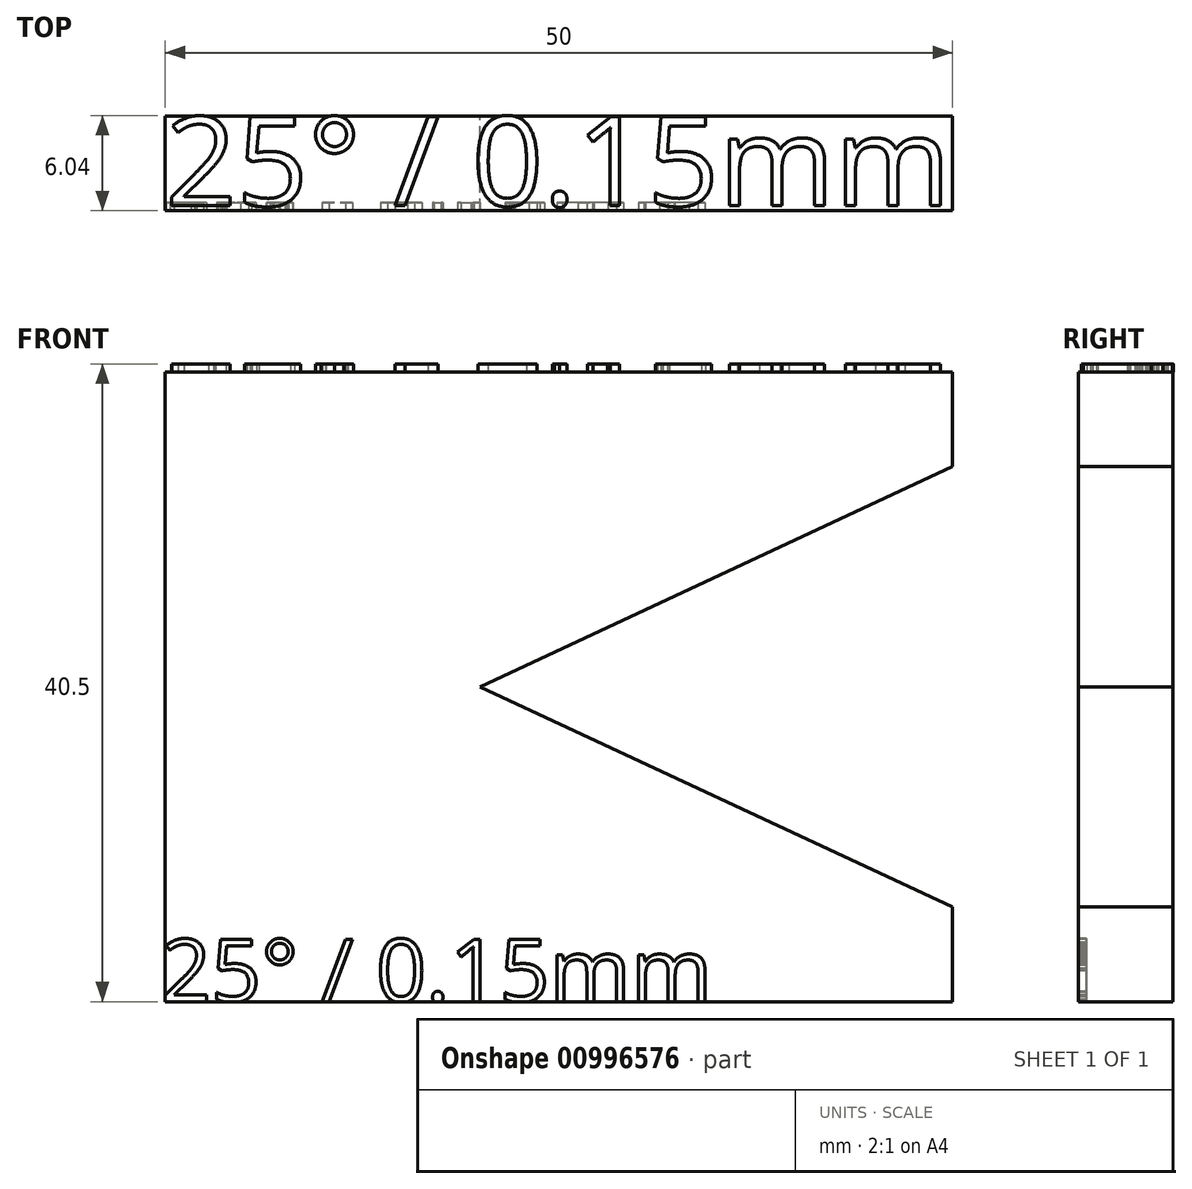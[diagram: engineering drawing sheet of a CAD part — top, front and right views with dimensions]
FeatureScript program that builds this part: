
annotation { "Feature Type Name" : "Feature", "Feature Type Description" : "" }
export const myFeature = defineFeature(function(context is Context, id is Id, definition is map)
    precondition{}
    {
        {
            var Q0;
            Q0=qCreatedBy(makeId("Front.planeOp"),FACE);
            var sketch = newSketch(context, id + "F0", { "sketchPlane" : qUnion([Q0])});
            skLineSegment(sketch, "E0", {"start": v(0, 39.45) * mm, "end": v(0, -35.1) * mm, "construction": true});
            skLineSegment(sketch, "E1", {"start": v(-35.77, 0) * mm, "end": v(35.97, 0) * mm, "construction": true});
            skLineSegment(sketch, "E2", {"start": v(-20, 20) * mm, "end": v(-20, -20) * mm});
            skLineSegment(sketch, "E3", {"start": v(-20, -20) * mm, "end": v(30, -20) * mm});
            skLineSegment(sketch, "E4", {"start": v(0, 0) * mm, "end": v(30, -13.99) * mm});
            skLineSegment(sketch, "E5", {"start": v(30, -13.99) * mm, "end": v(30, -20) * mm});
            skLineSegment(sketch, "E6.MirrorCS", {"start": v(0, 0) * mm, "end": v(30, 13.99) * mm});
            skLineSegment(sketch, "E7.MirrorCS", {"start": v(30, 13.99) * mm, "end": v(30, 20) * mm});
            skLineSegment(sketch, "E8.MirrorCS", {"start": v(-20, 20) * mm, "end": v(30, 20) * mm});
            skSolve(sketch);
        }
        {
            var Q0;
            Q0=makeQuery(id+"F0.imprint","IMPRINT",FACE,{"disambiguationData":[TD([[makeQuery(id+"F0.imprint","IMPRINT",EDGE,{"derivedFrom":sQuery(id+"F0.wireOp",EDGE,"E2")}),1.0]])]});
            extrude(context, id + "F1", {"entities" : qUnion([Q0]), "depth" : 6 * mm, "offsetDistance" : 25 * mm});
        }
        {
            var Q0;
            Q0=makeQuery(id+"F1.opExtrude","SWEPT_FACE",FACE,{"disambiguationData":[OSD([sQuery(id+"F0.wireOp",EDGE,"E8.MirrorCS")])]});
            var sketch = newSketch(context, id + "F2", { "sketchPlane" : qUnion([Q0])});
            skText(sketch, "E9", { "text": "25° / 0.15mm", "fontName": "OpenSans-Regular.ttf"});
            const initialGuessF2  = {"E9": [-0.02, -0.0057, 1, 0, 0.0057]};
            skSetInitialGuess(sketch, initialGuessF2);
            skSolve(sketch);
        }
        {
            var Q0;
            Q0=qSketchRegion(id+"F2",true);
            extrude(context, id + "F3", {"entities" : qUnion([Q0]), "operationType" : NewBodyOperationType.ADD, "depth" : 0.5 * mm, "offsetDistance" : 25 * mm});
        }
        {
            var Q0;
            Q0=makeQuery(id+"F1.opExtrude","SWEPT_FACE",FACE,{"disambiguationData":[OSD([sQuery(id+"F0.wireOp",EDGE,"E2")])]});
            var sketch = newSketch(context, id + "F4", { "sketchPlane" : qUnion([Q0])});
            skText(sketch, "E10", { "text": "25° / 0.15mm", "fontName": "OpenSans-Regular.ttf"});
            const initialGuessF4  = {"E10": [0, -0.024, 1, 0, 0.004]};
            skSetInitialGuess(sketch, initialGuessF4);
            skSolve(sketch);
        }
        {
            var Q0;
            Q0=qSketchRegion(id+"F4",true);
            extrude(context, id + "F5", {"entities" : qUnion([Q0]), "oppositeDirection" : true, "depth" : 0.5 * mm, "offsetDistance" : 25 * mm});
        }
        {
            var Q0;
            Q0=makeQuery(id+"F5.opExtrude","SWEPT_BODY",BODY,{"disambiguationData":[OSD([sQuery(id+"F4.wireOp",EDGE,"E10.sketch_text.stroke-0"),sQuery(id+"F4.wireOp",EDGE,"E10.sketch_text.stroke-1"),sQuery(id+"F4.wireOp",EDGE,"E10.sketch_text.stroke-2"),sQuery(id+"F4.wireOp",EDGE,"E10.sketch_text.stroke-3"),sQuery(id+"F4.wireOp",EDGE,"E10.sketch_text.stroke-4"),sQuery(id+"F4.wireOp",EDGE,"E10.sketch_text.stroke-5"),sQuery(id+"F4.wireOp",EDGE,"E10.sketch_text.stroke-6"),sQuery(id+"F4.wireOp",EDGE,"E10.sketch_text.stroke-7"),sQuery(id+"F4.wireOp",EDGE,"E10.sketch_text.stroke-8"),sQuery(id+"F4.wireOp",EDGE,"E10.sketch_text.stroke-9"),sQuery(id+"F4.wireOp",EDGE,"E10.sketch_text.stroke-10"),sQuery(id+"F4.wireOp",EDGE,"E10.sketch_text.stroke-11"),sQuery(id+"F4.wireOp",EDGE,"E10.sketch_text.stroke-12"),sQuery(id+"F4.wireOp",EDGE,"E10.sketch_text.stroke-13"),sQuery(id+"F4.wireOp",EDGE,"E10.sketch_text.stroke-14"),sQuery(id+"F4.wireOp",EDGE,"E10.sketch_text.stroke-15"),sQuery(id+"F4.wireOp",EDGE,"E10.sketch_text.stroke-16"),sQuery(id+"F4.wireOp",EDGE,"E10.sketch_text.stroke-17"),sQuery(id+"F4.wireOp",EDGE,"E10.sketch_text.stroke-18"),sQuery(id+"F4.wireOp",EDGE,"E10.sketch_text.stroke-19")])]});
            var Q1;
            Q1=makeQuery(id+"F5.opExtrude","SWEPT_BODY",BODY,{"disambiguationData":[OSD([sQuery(id+"F4.wireOp",EDGE,"E10.sketch_text.stroke-20"),sQuery(id+"F4.wireOp",EDGE,"E10.sketch_text.stroke-21"),sQuery(id+"F4.wireOp",EDGE,"E10.sketch_text.stroke-22"),sQuery(id+"F4.wireOp",EDGE,"E10.sketch_text.stroke-23"),sQuery(id+"F4.wireOp",EDGE,"E10.sketch_text.stroke-24"),sQuery(id+"F4.wireOp",EDGE,"E10.sketch_text.stroke-25"),sQuery(id+"F4.wireOp",EDGE,"E10.sketch_text.stroke-26"),sQuery(id+"F4.wireOp",EDGE,"E10.sketch_text.stroke-27"),sQuery(id+"F4.wireOp",EDGE,"E10.sketch_text.stroke-28"),sQuery(id+"F4.wireOp",EDGE,"E10.sketch_text.stroke-29"),sQuery(id+"F4.wireOp",EDGE,"E10.sketch_text.stroke-30"),sQuery(id+"F4.wireOp",EDGE,"E10.sketch_text.stroke-31"),sQuery(id+"F4.wireOp",EDGE,"E10.sketch_text.stroke-32"),sQuery(id+"F4.wireOp",EDGE,"E10.sketch_text.stroke-33"),sQuery(id+"F4.wireOp",EDGE,"E10.sketch_text.stroke-34"),sQuery(id+"F4.wireOp",EDGE,"E10.sketch_text.stroke-35"),sQuery(id+"F4.wireOp",EDGE,"E10.sketch_text.stroke-36"),sQuery(id+"F4.wireOp",EDGE,"E10.sketch_text.stroke-37"),sQuery(id+"F4.wireOp",EDGE,"E10.sketch_text.stroke-38")])]});
            var Q2;
            Q2=makeQuery(id+"F5.opExtrude","SWEPT_BODY",BODY,{"disambiguationData":[OSD([sQuery(id+"F4.wireOp",EDGE,"E10.sketch_text.stroke-39"),sQuery(id+"F4.wireOp",EDGE,"E10.sketch_text.stroke-40"),sQuery(id+"F4.wireOp",EDGE,"E10.sketch_text.stroke-41"),sQuery(id+"F4.wireOp",EDGE,"E10.sketch_text.stroke-42"),sQuery(id+"F4.wireOp",EDGE,"E10.sketch_text.stroke-43"),sQuery(id+"F4.wireOp",EDGE,"E10.sketch_text.stroke-44"),sQuery(id+"F4.wireOp",EDGE,"E10.sketch_text.stroke-45"),sQuery(id+"F4.wireOp",EDGE,"E10.sketch_text.stroke-46"),sQuery(id+"F4.wireOp",EDGE,"E10.sketch_text.stroke-47"),sQuery(id+"F4.wireOp",EDGE,"E10.sketch_text.stroke-48"),sQuery(id+"F4.wireOp",EDGE,"E10.sketch_text.stroke-49"),sQuery(id+"F4.wireOp",EDGE,"E10.sketch_text.stroke-50"),sQuery(id+"F4.wireOp",EDGE,"E10.sketch_text.stroke-51"),sQuery(id+"F4.wireOp",EDGE,"E10.sketch_text.stroke-52"),sQuery(id+"F4.wireOp",EDGE,"E10.sketch_text.stroke-53"),sQuery(id+"F4.wireOp",EDGE,"E10.sketch_text.stroke-54"),sQuery(id+"F4.wireOp",EDGE,"E10.sketch_text.stroke-55")])]});
            var Q3;
            Q3=makeQuery(id+"F5.opExtrude","SWEPT_BODY",BODY,{"disambiguationData":[OSD([sQuery(id+"F4.wireOp",EDGE,"E10.sketch_text.stroke-56"),sQuery(id+"F4.wireOp",EDGE,"E10.sketch_text.stroke-57"),sQuery(id+"F4.wireOp",EDGE,"E10.sketch_text.stroke-58"),sQuery(id+"F4.wireOp",EDGE,"E10.sketch_text.stroke-59")])]});
            var Q4;
            Q4=makeQuery(id+"F5.opExtrude","SWEPT_BODY",BODY,{"disambiguationData":[OSD([sQuery(id+"F4.wireOp",EDGE,"E10.sketch_text.stroke-60"),sQuery(id+"F4.wireOp",EDGE,"E10.sketch_text.stroke-61"),sQuery(id+"F4.wireOp",EDGE,"E10.sketch_text.stroke-62"),sQuery(id+"F4.wireOp",EDGE,"E10.sketch_text.stroke-63"),sQuery(id+"F4.wireOp",EDGE,"E10.sketch_text.stroke-64"),sQuery(id+"F4.wireOp",EDGE,"E10.sketch_text.stroke-65"),sQuery(id+"F4.wireOp",EDGE,"E10.sketch_text.stroke-66"),sQuery(id+"F4.wireOp",EDGE,"E10.sketch_text.stroke-67"),sQuery(id+"F4.wireOp",EDGE,"E10.sketch_text.stroke-68"),sQuery(id+"F4.wireOp",EDGE,"E10.sketch_text.stroke-69"),sQuery(id+"F4.wireOp",EDGE,"E10.sketch_text.stroke-70"),sQuery(id+"F4.wireOp",EDGE,"E10.sketch_text.stroke-71"),sQuery(id+"F4.wireOp",EDGE,"E10.sketch_text.stroke-72"),sQuery(id+"F4.wireOp",EDGE,"E10.sketch_text.stroke-73"),sQuery(id+"F4.wireOp",EDGE,"E10.sketch_text.stroke-74"),sQuery(id+"F4.wireOp",EDGE,"E10.sketch_text.stroke-75")])]});
            var Q5;
            Q5=makeQuery(id+"F5.opExtrude","SWEPT_BODY",BODY,{"disambiguationData":[OSD([sQuery(id+"F4.wireOp",EDGE,"E10.sketch_text.stroke-76"),sQuery(id+"F4.wireOp",EDGE,"E10.sketch_text.stroke-77"),sQuery(id+"F4.wireOp",EDGE,"E10.sketch_text.stroke-78"),sQuery(id+"F4.wireOp",EDGE,"E10.sketch_text.stroke-79"),sQuery(id+"F4.wireOp",EDGE,"E10.sketch_text.stroke-80"),sQuery(id+"F4.wireOp",EDGE,"E10.sketch_text.stroke-81"),sQuery(id+"F4.wireOp",EDGE,"E10.sketch_text.stroke-82"),sQuery(id+"F4.wireOp",EDGE,"E10.sketch_text.stroke-83")])]});
            var Q6;
            Q6=makeQuery(id+"F5.opExtrude","SWEPT_BODY",BODY,{"disambiguationData":[OSD([sQuery(id+"F4.wireOp",EDGE,"E10.sketch_text.stroke-84"),sQuery(id+"F4.wireOp",EDGE,"E10.sketch_text.stroke-85"),sQuery(id+"F4.wireOp",EDGE,"E10.sketch_text.stroke-86"),sQuery(id+"F4.wireOp",EDGE,"E10.sketch_text.stroke-87"),sQuery(id+"F4.wireOp",EDGE,"E10.sketch_text.stroke-88"),sQuery(id+"F4.wireOp",EDGE,"E10.sketch_text.stroke-89"),sQuery(id+"F4.wireOp",EDGE,"E10.sketch_text.stroke-90"),sQuery(id+"F4.wireOp",EDGE,"E10.sketch_text.stroke-91"),sQuery(id+"F4.wireOp",EDGE,"E10.sketch_text.stroke-92")])]});
            var Q7;
            Q7=makeQuery(id+"F5.opExtrude","SWEPT_BODY",BODY,{"disambiguationData":[OSD([sQuery(id+"F4.wireOp",EDGE,"E10.sketch_text.stroke-93"),sQuery(id+"F4.wireOp",EDGE,"E10.sketch_text.stroke-94"),sQuery(id+"F4.wireOp",EDGE,"E10.sketch_text.stroke-95"),sQuery(id+"F4.wireOp",EDGE,"E10.sketch_text.stroke-96"),sQuery(id+"F4.wireOp",EDGE,"E10.sketch_text.stroke-97"),sQuery(id+"F4.wireOp",EDGE,"E10.sketch_text.stroke-98"),sQuery(id+"F4.wireOp",EDGE,"E10.sketch_text.stroke-99"),sQuery(id+"F4.wireOp",EDGE,"E10.sketch_text.stroke-100"),sQuery(id+"F4.wireOp",EDGE,"E10.sketch_text.stroke-101"),sQuery(id+"F4.wireOp",EDGE,"E10.sketch_text.stroke-102"),sQuery(id+"F4.wireOp",EDGE,"E10.sketch_text.stroke-103"),sQuery(id+"F4.wireOp",EDGE,"E10.sketch_text.stroke-104"),sQuery(id+"F4.wireOp",EDGE,"E10.sketch_text.stroke-105"),sQuery(id+"F4.wireOp",EDGE,"E10.sketch_text.stroke-106"),sQuery(id+"F4.wireOp",EDGE,"E10.sketch_text.stroke-107"),sQuery(id+"F4.wireOp",EDGE,"E10.sketch_text.stroke-108"),sQuery(id+"F4.wireOp",EDGE,"E10.sketch_text.stroke-109"),sQuery(id+"F4.wireOp",EDGE,"E10.sketch_text.stroke-110"),sQuery(id+"F4.wireOp",EDGE,"E10.sketch_text.stroke-111"),sQuery(id+"F4.wireOp",EDGE,"E10.sketch_text.stroke-112"),sQuery(id+"F4.wireOp",EDGE,"E10.sketch_text.stroke-113"),sQuery(id+"F4.wireOp",EDGE,"E10.sketch_text.stroke-114"),sQuery(id+"F4.wireOp",EDGE,"E10.sketch_text.stroke-115"),sQuery(id+"F4.wireOp",EDGE,"E10.sketch_text.stroke-116"),sQuery(id+"F4.wireOp",EDGE,"E10.sketch_text.stroke-117"),sQuery(id+"F4.wireOp",EDGE,"E10.sketch_text.stroke-118"),sQuery(id+"F4.wireOp",EDGE,"E10.sketch_text.stroke-119"),sQuery(id+"F4.wireOp",EDGE,"E10.sketch_text.stroke-120")])]});
            var Q8;
            Q8=makeQuery(id+"F5.opExtrude","SWEPT_BODY",BODY,{"disambiguationData":[OSD([sQuery(id+"F4.wireOp",EDGE,"E10.sketch_text.stroke-121"),sQuery(id+"F4.wireOp",EDGE,"E10.sketch_text.stroke-122"),sQuery(id+"F4.wireOp",EDGE,"E10.sketch_text.stroke-123"),sQuery(id+"F4.wireOp",EDGE,"E10.sketch_text.stroke-124"),sQuery(id+"F4.wireOp",EDGE,"E10.sketch_text.stroke-125"),sQuery(id+"F4.wireOp",EDGE,"E10.sketch_text.stroke-126"),sQuery(id+"F4.wireOp",EDGE,"E10.sketch_text.stroke-127"),sQuery(id+"F4.wireOp",EDGE,"E10.sketch_text.stroke-128"),sQuery(id+"F4.wireOp",EDGE,"E10.sketch_text.stroke-129"),sQuery(id+"F4.wireOp",EDGE,"E10.sketch_text.stroke-130"),sQuery(id+"F4.wireOp",EDGE,"E10.sketch_text.stroke-131"),sQuery(id+"F4.wireOp",EDGE,"E10.sketch_text.stroke-132"),sQuery(id+"F4.wireOp",EDGE,"E10.sketch_text.stroke-133"),sQuery(id+"F4.wireOp",EDGE,"E10.sketch_text.stroke-134"),sQuery(id+"F4.wireOp",EDGE,"E10.sketch_text.stroke-135"),sQuery(id+"F4.wireOp",EDGE,"E10.sketch_text.stroke-136"),sQuery(id+"F4.wireOp",EDGE,"E10.sketch_text.stroke-137"),sQuery(id+"F4.wireOp",EDGE,"E10.sketch_text.stroke-138"),sQuery(id+"F4.wireOp",EDGE,"E10.sketch_text.stroke-139"),sQuery(id+"F4.wireOp",EDGE,"E10.sketch_text.stroke-140"),sQuery(id+"F4.wireOp",EDGE,"E10.sketch_text.stroke-141"),sQuery(id+"F4.wireOp",EDGE,"E10.sketch_text.stroke-142"),sQuery(id+"F4.wireOp",EDGE,"E10.sketch_text.stroke-143"),sQuery(id+"F4.wireOp",EDGE,"E10.sketch_text.stroke-144"),sQuery(id+"F4.wireOp",EDGE,"E10.sketch_text.stroke-145"),sQuery(id+"F4.wireOp",EDGE,"E10.sketch_text.stroke-146"),sQuery(id+"F4.wireOp",EDGE,"E10.sketch_text.stroke-147"),sQuery(id+"F4.wireOp",EDGE,"E10.sketch_text.stroke-148")])]});
            var Q9;
            Q9=makeQuery(id+"F5.opExtrude","SWEPT_BODY",BODY,{"disambiguationData":[OSD([sQuery(id+"F4.wireOp",EDGE,"E10.sketch_text.stroke-140"),sQuery(id+"F4.wireOp",EDGE,"E10.sketch_text.stroke-141"),sQuery(id+"F4.wireOp",EDGE,"E10.sketch_text.stroke-142"),sQuery(id+"F4.wireOp",EDGE,"E10.sketch_text.stroke-143"),sQuery(id+"F4.wireOp",EDGE,"E10.sketch_text.stroke-144"),sQuery(id+"F4.wireOp",EDGE,"E10.sketch_text.stroke-145"),sQuery(id+"F4.wireOp",EDGE,"E10.sketch_text.stroke-146"),sQuery(id+"F4.wireOp",EDGE,"E10.sketch_text.stroke-147"),sQuery(id+"F4.wireOp",EDGE,"E10.sketch_text.stroke-148"),sQuery(id+"F4.wireOp",EDGE,"E10.sketch_text.stroke-149"),sQuery(id+"F4.wireOp",EDGE,"E10.sketch_text.stroke-150"),sQuery(id+"F4.wireOp",EDGE,"E10.sketch_text.stroke-151"),sQuery(id+"F4.wireOp",EDGE,"E10.sketch_text.stroke-152"),sQuery(id+"F4.wireOp",EDGE,"E10.sketch_text.stroke-153"),sQuery(id+"F4.wireOp",EDGE,"E10.sketch_text.stroke-154"),sQuery(id+"F4.wireOp",EDGE,"E10.sketch_text.stroke-155"),sQuery(id+"F4.wireOp",EDGE,"E10.sketch_text.stroke-156"),sQuery(id+"F4.wireOp",EDGE,"E10.sketch_text.stroke-157"),sQuery(id+"F4.wireOp",EDGE,"E10.sketch_text.stroke-158"),sQuery(id+"F4.wireOp",EDGE,"E10.sketch_text.stroke-159"),sQuery(id+"F4.wireOp",EDGE,"E10.sketch_text.stroke-160"),sQuery(id+"F4.wireOp",EDGE,"E10.sketch_text.stroke-161"),sQuery(id+"F4.wireOp",EDGE,"E10.sketch_text.stroke-162"),sQuery(id+"F4.wireOp",EDGE,"E10.sketch_text.stroke-163"),sQuery(id+"F4.wireOp",EDGE,"E10.sketch_text.stroke-164"),sQuery(id+"F4.wireOp",EDGE,"E10.sketch_text.stroke-165"),sQuery(id+"F4.wireOp",EDGE,"E10.sketch_text.stroke-166"),sQuery(id+"F4.wireOp",EDGE,"E10.sketch_text.stroke-167")])]});
            var Q10;
            Q10=makeQuery(id+"F1.opExtrude","CAP_EDGE",EDGE,{"disambiguationData":[OSD([sQuery(id+"F0.wireOp",EDGE,"E2")])],"isStart":false});
            transform(context, id + "F6", {"entities" : qUnion([Q0, Q1, Q2, Q3, Q4, Q5, Q6, Q7, Q8, Q9]), "transformType" : TransformType.ROTATION, "transformAxis" : qUnion([Q10]), "angle" : 90 * degree, "oppositeDirection" : true, "makeCopy" : false});
        }
        {
            var Q0;
            Q0=makeQuery(id+"F5.opExtrude","SWEPT_BODY",BODY,{"disambiguationData":[OSD([sQuery(id+"F4.wireOp",EDGE,"E10.sketch_text.stroke-84"),sQuery(id+"F4.wireOp",EDGE,"E10.sketch_text.stroke-85"),sQuery(id+"F4.wireOp",EDGE,"E10.sketch_text.stroke-86"),sQuery(id+"F4.wireOp",EDGE,"E10.sketch_text.stroke-87"),sQuery(id+"F4.wireOp",EDGE,"E10.sketch_text.stroke-88"),sQuery(id+"F4.wireOp",EDGE,"E10.sketch_text.stroke-89"),sQuery(id+"F4.wireOp",EDGE,"E10.sketch_text.stroke-90"),sQuery(id+"F4.wireOp",EDGE,"E10.sketch_text.stroke-91"),sQuery(id+"F4.wireOp",EDGE,"E10.sketch_text.stroke-92")])]});
            var Q1;
            Q1=makeQuery(id+"F5.opExtrude","SWEPT_BODY",BODY,{"disambiguationData":[OSD([sQuery(id+"F4.wireOp",EDGE,"E10.sketch_text.stroke-56"),sQuery(id+"F4.wireOp",EDGE,"E10.sketch_text.stroke-57"),sQuery(id+"F4.wireOp",EDGE,"E10.sketch_text.stroke-58"),sQuery(id+"F4.wireOp",EDGE,"E10.sketch_text.stroke-59")])]});
            var Q2;
            Q2=makeQuery(id+"F5.opExtrude","SWEPT_BODY",BODY,{"disambiguationData":[OSD([sQuery(id+"F4.wireOp",EDGE,"E10.sketch_text.stroke-60"),sQuery(id+"F4.wireOp",EDGE,"E10.sketch_text.stroke-61"),sQuery(id+"F4.wireOp",EDGE,"E10.sketch_text.stroke-62"),sQuery(id+"F4.wireOp",EDGE,"E10.sketch_text.stroke-63"),sQuery(id+"F4.wireOp",EDGE,"E10.sketch_text.stroke-64"),sQuery(id+"F4.wireOp",EDGE,"E10.sketch_text.stroke-65"),sQuery(id+"F4.wireOp",EDGE,"E10.sketch_text.stroke-66"),sQuery(id+"F4.wireOp",EDGE,"E10.sketch_text.stroke-67"),sQuery(id+"F4.wireOp",EDGE,"E10.sketch_text.stroke-68"),sQuery(id+"F4.wireOp",EDGE,"E10.sketch_text.stroke-69"),sQuery(id+"F4.wireOp",EDGE,"E10.sketch_text.stroke-70"),sQuery(id+"F4.wireOp",EDGE,"E10.sketch_text.stroke-71"),sQuery(id+"F4.wireOp",EDGE,"E10.sketch_text.stroke-72"),sQuery(id+"F4.wireOp",EDGE,"E10.sketch_text.stroke-73"),sQuery(id+"F4.wireOp",EDGE,"E10.sketch_text.stroke-74"),sQuery(id+"F4.wireOp",EDGE,"E10.sketch_text.stroke-75")])]});
            var Q3;
            Q3=makeQuery(id+"F5.opExtrude","SWEPT_BODY",BODY,{"disambiguationData":[OSD([sQuery(id+"F4.wireOp",EDGE,"E10.sketch_text.stroke-76"),sQuery(id+"F4.wireOp",EDGE,"E10.sketch_text.stroke-77"),sQuery(id+"F4.wireOp",EDGE,"E10.sketch_text.stroke-78"),sQuery(id+"F4.wireOp",EDGE,"E10.sketch_text.stroke-79"),sQuery(id+"F4.wireOp",EDGE,"E10.sketch_text.stroke-80"),sQuery(id+"F4.wireOp",EDGE,"E10.sketch_text.stroke-81"),sQuery(id+"F4.wireOp",EDGE,"E10.sketch_text.stroke-82"),sQuery(id+"F4.wireOp",EDGE,"E10.sketch_text.stroke-83")])]});
            var Q4;
            Q4=makeQuery(id+"F5.opExtrude","SWEPT_BODY",BODY,{"disambiguationData":[OSD([sQuery(id+"F4.wireOp",EDGE,"E10.sketch_text.stroke-0"),sQuery(id+"F4.wireOp",EDGE,"E10.sketch_text.stroke-1"),sQuery(id+"F4.wireOp",EDGE,"E10.sketch_text.stroke-2"),sQuery(id+"F4.wireOp",EDGE,"E10.sketch_text.stroke-3"),sQuery(id+"F4.wireOp",EDGE,"E10.sketch_text.stroke-4"),sQuery(id+"F4.wireOp",EDGE,"E10.sketch_text.stroke-5"),sQuery(id+"F4.wireOp",EDGE,"E10.sketch_text.stroke-6"),sQuery(id+"F4.wireOp",EDGE,"E10.sketch_text.stroke-7"),sQuery(id+"F4.wireOp",EDGE,"E10.sketch_text.stroke-8"),sQuery(id+"F4.wireOp",EDGE,"E10.sketch_text.stroke-9"),sQuery(id+"F4.wireOp",EDGE,"E10.sketch_text.stroke-10"),sQuery(id+"F4.wireOp",EDGE,"E10.sketch_text.stroke-11"),sQuery(id+"F4.wireOp",EDGE,"E10.sketch_text.stroke-12"),sQuery(id+"F4.wireOp",EDGE,"E10.sketch_text.stroke-13"),sQuery(id+"F4.wireOp",EDGE,"E10.sketch_text.stroke-14"),sQuery(id+"F4.wireOp",EDGE,"E10.sketch_text.stroke-15"),sQuery(id+"F4.wireOp",EDGE,"E10.sketch_text.stroke-16"),sQuery(id+"F4.wireOp",EDGE,"E10.sketch_text.stroke-17"),sQuery(id+"F4.wireOp",EDGE,"E10.sketch_text.stroke-18"),sQuery(id+"F4.wireOp",EDGE,"E10.sketch_text.stroke-19")])]});
            var Q5;
            Q5=makeQuery(id+"F5.opExtrude","SWEPT_BODY",BODY,{"disambiguationData":[OSD([sQuery(id+"F4.wireOp",EDGE,"E10.sketch_text.stroke-20"),sQuery(id+"F4.wireOp",EDGE,"E10.sketch_text.stroke-21"),sQuery(id+"F4.wireOp",EDGE,"E10.sketch_text.stroke-22"),sQuery(id+"F4.wireOp",EDGE,"E10.sketch_text.stroke-23"),sQuery(id+"F4.wireOp",EDGE,"E10.sketch_text.stroke-24"),sQuery(id+"F4.wireOp",EDGE,"E10.sketch_text.stroke-25"),sQuery(id+"F4.wireOp",EDGE,"E10.sketch_text.stroke-26"),sQuery(id+"F4.wireOp",EDGE,"E10.sketch_text.stroke-27"),sQuery(id+"F4.wireOp",EDGE,"E10.sketch_text.stroke-28"),sQuery(id+"F4.wireOp",EDGE,"E10.sketch_text.stroke-29"),sQuery(id+"F4.wireOp",EDGE,"E10.sketch_text.stroke-30"),sQuery(id+"F4.wireOp",EDGE,"E10.sketch_text.stroke-31"),sQuery(id+"F4.wireOp",EDGE,"E10.sketch_text.stroke-32"),sQuery(id+"F4.wireOp",EDGE,"E10.sketch_text.stroke-33"),sQuery(id+"F4.wireOp",EDGE,"E10.sketch_text.stroke-34"),sQuery(id+"F4.wireOp",EDGE,"E10.sketch_text.stroke-35"),sQuery(id+"F4.wireOp",EDGE,"E10.sketch_text.stroke-36"),sQuery(id+"F4.wireOp",EDGE,"E10.sketch_text.stroke-37"),sQuery(id+"F4.wireOp",EDGE,"E10.sketch_text.stroke-38")])]});
            var Q6;
            Q6=makeQuery(id+"F5.opExtrude","SWEPT_BODY",BODY,{"disambiguationData":[OSD([sQuery(id+"F4.wireOp",EDGE,"E10.sketch_text.stroke-39"),sQuery(id+"F4.wireOp",EDGE,"E10.sketch_text.stroke-40"),sQuery(id+"F4.wireOp",EDGE,"E10.sketch_text.stroke-41"),sQuery(id+"F4.wireOp",EDGE,"E10.sketch_text.stroke-42"),sQuery(id+"F4.wireOp",EDGE,"E10.sketch_text.stroke-43"),sQuery(id+"F4.wireOp",EDGE,"E10.sketch_text.stroke-44"),sQuery(id+"F4.wireOp",EDGE,"E10.sketch_text.stroke-45"),sQuery(id+"F4.wireOp",EDGE,"E10.sketch_text.stroke-46"),sQuery(id+"F4.wireOp",EDGE,"E10.sketch_text.stroke-47"),sQuery(id+"F4.wireOp",EDGE,"E10.sketch_text.stroke-48"),sQuery(id+"F4.wireOp",EDGE,"E10.sketch_text.stroke-49"),sQuery(id+"F4.wireOp",EDGE,"E10.sketch_text.stroke-50"),sQuery(id+"F4.wireOp",EDGE,"E10.sketch_text.stroke-51"),sQuery(id+"F4.wireOp",EDGE,"E10.sketch_text.stroke-52"),sQuery(id+"F4.wireOp",EDGE,"E10.sketch_text.stroke-53"),sQuery(id+"F4.wireOp",EDGE,"E10.sketch_text.stroke-54"),sQuery(id+"F4.wireOp",EDGE,"E10.sketch_text.stroke-55")])]});
            var Q7;
            Q7=makeQuery(id+"F5.opExtrude","SWEPT_BODY",BODY,{"disambiguationData":[OSD([sQuery(id+"F4.wireOp",EDGE,"E10.sketch_text.stroke-140"),sQuery(id+"F4.wireOp",EDGE,"E10.sketch_text.stroke-141"),sQuery(id+"F4.wireOp",EDGE,"E10.sketch_text.stroke-142"),sQuery(id+"F4.wireOp",EDGE,"E10.sketch_text.stroke-143"),sQuery(id+"F4.wireOp",EDGE,"E10.sketch_text.stroke-144"),sQuery(id+"F4.wireOp",EDGE,"E10.sketch_text.stroke-145"),sQuery(id+"F4.wireOp",EDGE,"E10.sketch_text.stroke-146"),sQuery(id+"F4.wireOp",EDGE,"E10.sketch_text.stroke-147"),sQuery(id+"F4.wireOp",EDGE,"E10.sketch_text.stroke-148"),sQuery(id+"F4.wireOp",EDGE,"E10.sketch_text.stroke-149"),sQuery(id+"F4.wireOp",EDGE,"E10.sketch_text.stroke-150"),sQuery(id+"F4.wireOp",EDGE,"E10.sketch_text.stroke-151"),sQuery(id+"F4.wireOp",EDGE,"E10.sketch_text.stroke-152"),sQuery(id+"F4.wireOp",EDGE,"E10.sketch_text.stroke-153"),sQuery(id+"F4.wireOp",EDGE,"E10.sketch_text.stroke-154"),sQuery(id+"F4.wireOp",EDGE,"E10.sketch_text.stroke-155"),sQuery(id+"F4.wireOp",EDGE,"E10.sketch_text.stroke-156"),sQuery(id+"F4.wireOp",EDGE,"E10.sketch_text.stroke-157"),sQuery(id+"F4.wireOp",EDGE,"E10.sketch_text.stroke-158"),sQuery(id+"F4.wireOp",EDGE,"E10.sketch_text.stroke-159"),sQuery(id+"F4.wireOp",EDGE,"E10.sketch_text.stroke-160"),sQuery(id+"F4.wireOp",EDGE,"E10.sketch_text.stroke-161"),sQuery(id+"F4.wireOp",EDGE,"E10.sketch_text.stroke-162"),sQuery(id+"F4.wireOp",EDGE,"E10.sketch_text.stroke-163"),sQuery(id+"F4.wireOp",EDGE,"E10.sketch_text.stroke-164"),sQuery(id+"F4.wireOp",EDGE,"E10.sketch_text.stroke-165"),sQuery(id+"F4.wireOp",EDGE,"E10.sketch_text.stroke-166"),sQuery(id+"F4.wireOp",EDGE,"E10.sketch_text.stroke-167")])]});
            var Q8;
            Q8=makeQuery(id+"F5.opExtrude","SWEPT_BODY",BODY,{"disambiguationData":[OSD([sQuery(id+"F4.wireOp",EDGE,"E10.sketch_text.stroke-112"),sQuery(id+"F4.wireOp",EDGE,"E10.sketch_text.stroke-113"),sQuery(id+"F4.wireOp",EDGE,"E10.sketch_text.stroke-114"),sQuery(id+"F4.wireOp",EDGE,"E10.sketch_text.stroke-115"),sQuery(id+"F4.wireOp",EDGE,"E10.sketch_text.stroke-116"),sQuery(id+"F4.wireOp",EDGE,"E10.sketch_text.stroke-117"),sQuery(id+"F4.wireOp",EDGE,"E10.sketch_text.stroke-118"),sQuery(id+"F4.wireOp",EDGE,"E10.sketch_text.stroke-119"),sQuery(id+"F4.wireOp",EDGE,"E10.sketch_text.stroke-120"),sQuery(id+"F4.wireOp",EDGE,"E10.sketch_text.stroke-121"),sQuery(id+"F4.wireOp",EDGE,"E10.sketch_text.stroke-122"),sQuery(id+"F4.wireOp",EDGE,"E10.sketch_text.stroke-123"),sQuery(id+"F4.wireOp",EDGE,"E10.sketch_text.stroke-124"),sQuery(id+"F4.wireOp",EDGE,"E10.sketch_text.stroke-125"),sQuery(id+"F4.wireOp",EDGE,"E10.sketch_text.stroke-126"),sQuery(id+"F4.wireOp",EDGE,"E10.sketch_text.stroke-127"),sQuery(id+"F4.wireOp",EDGE,"E10.sketch_text.stroke-128"),sQuery(id+"F4.wireOp",EDGE,"E10.sketch_text.stroke-129"),sQuery(id+"F4.wireOp",EDGE,"E10.sketch_text.stroke-130"),sQuery(id+"F4.wireOp",EDGE,"E10.sketch_text.stroke-131"),sQuery(id+"F4.wireOp",EDGE,"E10.sketch_text.stroke-132"),sQuery(id+"F4.wireOp",EDGE,"E10.sketch_text.stroke-133"),sQuery(id+"F4.wireOp",EDGE,"E10.sketch_text.stroke-134"),sQuery(id+"F4.wireOp",EDGE,"E10.sketch_text.stroke-135"),sQuery(id+"F4.wireOp",EDGE,"E10.sketch_text.stroke-136"),sQuery(id+"F4.wireOp",EDGE,"E10.sketch_text.stroke-137"),sQuery(id+"F4.wireOp",EDGE,"E10.sketch_text.stroke-138"),sQuery(id+"F4.wireOp",EDGE,"E10.sketch_text.stroke-139")])]});
            var Q9;
            Q9=makeQuery(id+"F5.opExtrude","SWEPT_BODY",BODY,{"disambiguationData":[OSD([sQuery(id+"F4.wireOp",EDGE,"E10.sketch_text.stroke-93"),sQuery(id+"F4.wireOp",EDGE,"E10.sketch_text.stroke-94"),sQuery(id+"F4.wireOp",EDGE,"E10.sketch_text.stroke-95"),sQuery(id+"F4.wireOp",EDGE,"E10.sketch_text.stroke-96"),sQuery(id+"F4.wireOp",EDGE,"E10.sketch_text.stroke-97"),sQuery(id+"F4.wireOp",EDGE,"E10.sketch_text.stroke-98"),sQuery(id+"F4.wireOp",EDGE,"E10.sketch_text.stroke-99"),sQuery(id+"F4.wireOp",EDGE,"E10.sketch_text.stroke-100"),sQuery(id+"F4.wireOp",EDGE,"E10.sketch_text.stroke-101"),sQuery(id+"F4.wireOp",EDGE,"E10.sketch_text.stroke-102"),sQuery(id+"F4.wireOp",EDGE,"E10.sketch_text.stroke-103"),sQuery(id+"F4.wireOp",EDGE,"E10.sketch_text.stroke-104"),sQuery(id+"F4.wireOp",EDGE,"E10.sketch_text.stroke-105"),sQuery(id+"F4.wireOp",EDGE,"E10.sketch_text.stroke-106"),sQuery(id+"F4.wireOp",EDGE,"E10.sketch_text.stroke-107"),sQuery(id+"F4.wireOp",EDGE,"E10.sketch_text.stroke-108"),sQuery(id+"F4.wireOp",EDGE,"E10.sketch_text.stroke-109"),sQuery(id+"F4.wireOp",EDGE,"E10.sketch_text.stroke-110"),sQuery(id+"F4.wireOp",EDGE,"E10.sketch_text.stroke-111")])]});
            var Q10;
            Q10=makeQuery(id+"F5.opExtrude","CAP_VERTEX",VERTEX,{"disambiguationData":[OSD([sQuery(id+"F4.wireOp",EDGE,"E10.sketch_text.stroke-0"),sQuery(id+"F4.wireOp",EDGE,"E10.sketch_text.stroke-1")])],"isStart":true});
            var Q11;
            Q11=makeQuery(id+"F1.opExtrude","CAP_VERTEX",VERTEX,{"disambiguationData":[OSD([sQuery(id+"F0.wireOp",EDGE,"E2"),sQuery(id+"F0.wireOp",EDGE,"E3")])],"isStart":false});
            transform(context, id + "F7", {"entities" : qUnion([Q0, Q1, Q2, Q3, Q4, Q5, Q6, Q7, Q8, Q9]), "transformType" : TransformType.TRANSLATION_ENTITY, "oppositeDirectionEntity" : false, "transformLine" : qUnion([Q10, Q11]), "makeCopy" : false});
        }
        {
            var Q0;
            Q0=makeQuery(id+"F5.opExtrude","SWEPT_BODY",BODY,{"disambiguationData":[OSD([sQuery(id+"F4.wireOp",EDGE,"E10.sketch_text.stroke-0"),sQuery(id+"F4.wireOp",EDGE,"E10.sketch_text.stroke-1"),sQuery(id+"F4.wireOp",EDGE,"E10.sketch_text.stroke-2"),sQuery(id+"F4.wireOp",EDGE,"E10.sketch_text.stroke-3"),sQuery(id+"F4.wireOp",EDGE,"E10.sketch_text.stroke-4"),sQuery(id+"F4.wireOp",EDGE,"E10.sketch_text.stroke-5"),sQuery(id+"F4.wireOp",EDGE,"E10.sketch_text.stroke-6"),sQuery(id+"F4.wireOp",EDGE,"E10.sketch_text.stroke-7"),sQuery(id+"F4.wireOp",EDGE,"E10.sketch_text.stroke-8"),sQuery(id+"F4.wireOp",EDGE,"E10.sketch_text.stroke-9"),sQuery(id+"F4.wireOp",EDGE,"E10.sketch_text.stroke-10"),sQuery(id+"F4.wireOp",EDGE,"E10.sketch_text.stroke-11"),sQuery(id+"F4.wireOp",EDGE,"E10.sketch_text.stroke-12"),sQuery(id+"F4.wireOp",EDGE,"E10.sketch_text.stroke-13"),sQuery(id+"F4.wireOp",EDGE,"E10.sketch_text.stroke-14"),sQuery(id+"F4.wireOp",EDGE,"E10.sketch_text.stroke-15"),sQuery(id+"F4.wireOp",EDGE,"E10.sketch_text.stroke-16"),sQuery(id+"F4.wireOp",EDGE,"E10.sketch_text.stroke-17"),sQuery(id+"F4.wireOp",EDGE,"E10.sketch_text.stroke-18"),sQuery(id+"F4.wireOp",EDGE,"E10.sketch_text.stroke-19")])]});
            var Q1;
            Q1=makeQuery(id+"F5.opExtrude","SWEPT_BODY",BODY,{"disambiguationData":[OSD([sQuery(id+"F4.wireOp",EDGE,"E10.sketch_text.stroke-20"),sQuery(id+"F4.wireOp",EDGE,"E10.sketch_text.stroke-21"),sQuery(id+"F4.wireOp",EDGE,"E10.sketch_text.stroke-22"),sQuery(id+"F4.wireOp",EDGE,"E10.sketch_text.stroke-23"),sQuery(id+"F4.wireOp",EDGE,"E10.sketch_text.stroke-24"),sQuery(id+"F4.wireOp",EDGE,"E10.sketch_text.stroke-25"),sQuery(id+"F4.wireOp",EDGE,"E10.sketch_text.stroke-26"),sQuery(id+"F4.wireOp",EDGE,"E10.sketch_text.stroke-27"),sQuery(id+"F4.wireOp",EDGE,"E10.sketch_text.stroke-28"),sQuery(id+"F4.wireOp",EDGE,"E10.sketch_text.stroke-29"),sQuery(id+"F4.wireOp",EDGE,"E10.sketch_text.stroke-30"),sQuery(id+"F4.wireOp",EDGE,"E10.sketch_text.stroke-31"),sQuery(id+"F4.wireOp",EDGE,"E10.sketch_text.stroke-32"),sQuery(id+"F4.wireOp",EDGE,"E10.sketch_text.stroke-33"),sQuery(id+"F4.wireOp",EDGE,"E10.sketch_text.stroke-34"),sQuery(id+"F4.wireOp",EDGE,"E10.sketch_text.stroke-35"),sQuery(id+"F4.wireOp",EDGE,"E10.sketch_text.stroke-36"),sQuery(id+"F4.wireOp",EDGE,"E10.sketch_text.stroke-37"),sQuery(id+"F4.wireOp",EDGE,"E10.sketch_text.stroke-38")])]});
            var Q2;
            Q2=makeQuery(id+"F5.opExtrude","SWEPT_BODY",BODY,{"disambiguationData":[OSD([sQuery(id+"F4.wireOp",EDGE,"E10.sketch_text.stroke-39"),sQuery(id+"F4.wireOp",EDGE,"E10.sketch_text.stroke-40"),sQuery(id+"F4.wireOp",EDGE,"E10.sketch_text.stroke-41"),sQuery(id+"F4.wireOp",EDGE,"E10.sketch_text.stroke-42"),sQuery(id+"F4.wireOp",EDGE,"E10.sketch_text.stroke-43"),sQuery(id+"F4.wireOp",EDGE,"E10.sketch_text.stroke-44"),sQuery(id+"F4.wireOp",EDGE,"E10.sketch_text.stroke-45"),sQuery(id+"F4.wireOp",EDGE,"E10.sketch_text.stroke-46"),sQuery(id+"F4.wireOp",EDGE,"E10.sketch_text.stroke-47"),sQuery(id+"F4.wireOp",EDGE,"E10.sketch_text.stroke-48"),sQuery(id+"F4.wireOp",EDGE,"E10.sketch_text.stroke-49"),sQuery(id+"F4.wireOp",EDGE,"E10.sketch_text.stroke-50"),sQuery(id+"F4.wireOp",EDGE,"E10.sketch_text.stroke-51"),sQuery(id+"F4.wireOp",EDGE,"E10.sketch_text.stroke-52"),sQuery(id+"F4.wireOp",EDGE,"E10.sketch_text.stroke-53"),sQuery(id+"F4.wireOp",EDGE,"E10.sketch_text.stroke-54"),sQuery(id+"F4.wireOp",EDGE,"E10.sketch_text.stroke-55")])]});
            var Q3;
            Q3=makeQuery(id+"F5.opExtrude","SWEPT_BODY",BODY,{"disambiguationData":[OSD([sQuery(id+"F4.wireOp",EDGE,"E10.sketch_text.stroke-56"),sQuery(id+"F4.wireOp",EDGE,"E10.sketch_text.stroke-57"),sQuery(id+"F4.wireOp",EDGE,"E10.sketch_text.stroke-58"),sQuery(id+"F4.wireOp",EDGE,"E10.sketch_text.stroke-59")])]});
            var Q4;
            Q4=makeQuery(id+"F5.opExtrude","SWEPT_BODY",BODY,{"disambiguationData":[OSD([sQuery(id+"F4.wireOp",EDGE,"E10.sketch_text.stroke-60"),sQuery(id+"F4.wireOp",EDGE,"E10.sketch_text.stroke-61"),sQuery(id+"F4.wireOp",EDGE,"E10.sketch_text.stroke-62"),sQuery(id+"F4.wireOp",EDGE,"E10.sketch_text.stroke-63"),sQuery(id+"F4.wireOp",EDGE,"E10.sketch_text.stroke-64"),sQuery(id+"F4.wireOp",EDGE,"E10.sketch_text.stroke-65"),sQuery(id+"F4.wireOp",EDGE,"E10.sketch_text.stroke-66"),sQuery(id+"F4.wireOp",EDGE,"E10.sketch_text.stroke-67"),sQuery(id+"F4.wireOp",EDGE,"E10.sketch_text.stroke-68"),sQuery(id+"F4.wireOp",EDGE,"E10.sketch_text.stroke-69"),sQuery(id+"F4.wireOp",EDGE,"E10.sketch_text.stroke-70"),sQuery(id+"F4.wireOp",EDGE,"E10.sketch_text.stroke-71"),sQuery(id+"F4.wireOp",EDGE,"E10.sketch_text.stroke-72"),sQuery(id+"F4.wireOp",EDGE,"E10.sketch_text.stroke-73"),sQuery(id+"F4.wireOp",EDGE,"E10.sketch_text.stroke-74"),sQuery(id+"F4.wireOp",EDGE,"E10.sketch_text.stroke-75")])]});
            var Q5;
            Q5=makeQuery(id+"F5.opExtrude","SWEPT_BODY",BODY,{"disambiguationData":[OSD([sQuery(id+"F4.wireOp",EDGE,"E10.sketch_text.stroke-76"),sQuery(id+"F4.wireOp",EDGE,"E10.sketch_text.stroke-77"),sQuery(id+"F4.wireOp",EDGE,"E10.sketch_text.stroke-78"),sQuery(id+"F4.wireOp",EDGE,"E10.sketch_text.stroke-79"),sQuery(id+"F4.wireOp",EDGE,"E10.sketch_text.stroke-80"),sQuery(id+"F4.wireOp",EDGE,"E10.sketch_text.stroke-81"),sQuery(id+"F4.wireOp",EDGE,"E10.sketch_text.stroke-82"),sQuery(id+"F4.wireOp",EDGE,"E10.sketch_text.stroke-83")])]});
            var Q6;
            Q6=makeQuery(id+"F5.opExtrude","SWEPT_BODY",BODY,{"disambiguationData":[OSD([sQuery(id+"F4.wireOp",EDGE,"E10.sketch_text.stroke-84"),sQuery(id+"F4.wireOp",EDGE,"E10.sketch_text.stroke-85"),sQuery(id+"F4.wireOp",EDGE,"E10.sketch_text.stroke-86"),sQuery(id+"F4.wireOp",EDGE,"E10.sketch_text.stroke-87"),sQuery(id+"F4.wireOp",EDGE,"E10.sketch_text.stroke-88"),sQuery(id+"F4.wireOp",EDGE,"E10.sketch_text.stroke-89"),sQuery(id+"F4.wireOp",EDGE,"E10.sketch_text.stroke-90"),sQuery(id+"F4.wireOp",EDGE,"E10.sketch_text.stroke-91"),sQuery(id+"F4.wireOp",EDGE,"E10.sketch_text.stroke-92")])]});
            var Q7;
            Q7=makeQuery(id+"F5.opExtrude","SWEPT_BODY",BODY,{"disambiguationData":[OSD([sQuery(id+"F4.wireOp",EDGE,"E10.sketch_text.stroke-93"),sQuery(id+"F4.wireOp",EDGE,"E10.sketch_text.stroke-94"),sQuery(id+"F4.wireOp",EDGE,"E10.sketch_text.stroke-95"),sQuery(id+"F4.wireOp",EDGE,"E10.sketch_text.stroke-96"),sQuery(id+"F4.wireOp",EDGE,"E10.sketch_text.stroke-97"),sQuery(id+"F4.wireOp",EDGE,"E10.sketch_text.stroke-98"),sQuery(id+"F4.wireOp",EDGE,"E10.sketch_text.stroke-99"),sQuery(id+"F4.wireOp",EDGE,"E10.sketch_text.stroke-100"),sQuery(id+"F4.wireOp",EDGE,"E10.sketch_text.stroke-101"),sQuery(id+"F4.wireOp",EDGE,"E10.sketch_text.stroke-102"),sQuery(id+"F4.wireOp",EDGE,"E10.sketch_text.stroke-103"),sQuery(id+"F4.wireOp",EDGE,"E10.sketch_text.stroke-104"),sQuery(id+"F4.wireOp",EDGE,"E10.sketch_text.stroke-105"),sQuery(id+"F4.wireOp",EDGE,"E10.sketch_text.stroke-106"),sQuery(id+"F4.wireOp",EDGE,"E10.sketch_text.stroke-107"),sQuery(id+"F4.wireOp",EDGE,"E10.sketch_text.stroke-108"),sQuery(id+"F4.wireOp",EDGE,"E10.sketch_text.stroke-109"),sQuery(id+"F4.wireOp",EDGE,"E10.sketch_text.stroke-110"),sQuery(id+"F4.wireOp",EDGE,"E10.sketch_text.stroke-111"),sQuery(id+"F4.wireOp",EDGE,"E10.sketch_text.stroke-112"),sQuery(id+"F4.wireOp",EDGE,"E10.sketch_text.stroke-113"),sQuery(id+"F4.wireOp",EDGE,"E10.sketch_text.stroke-114"),sQuery(id+"F4.wireOp",EDGE,"E10.sketch_text.stroke-115"),sQuery(id+"F4.wireOp",EDGE,"E10.sketch_text.stroke-116"),sQuery(id+"F4.wireOp",EDGE,"E10.sketch_text.stroke-117"),sQuery(id+"F4.wireOp",EDGE,"E10.sketch_text.stroke-118"),sQuery(id+"F4.wireOp",EDGE,"E10.sketch_text.stroke-119"),sQuery(id+"F4.wireOp",EDGE,"E10.sketch_text.stroke-120")])]});
            var Q8;
            Q8=makeQuery(id+"F5.opExtrude","SWEPT_BODY",BODY,{"disambiguationData":[OSD([sQuery(id+"F4.wireOp",EDGE,"E10.sketch_text.stroke-121"),sQuery(id+"F4.wireOp",EDGE,"E10.sketch_text.stroke-122"),sQuery(id+"F4.wireOp",EDGE,"E10.sketch_text.stroke-123"),sQuery(id+"F4.wireOp",EDGE,"E10.sketch_text.stroke-124"),sQuery(id+"F4.wireOp",EDGE,"E10.sketch_text.stroke-125"),sQuery(id+"F4.wireOp",EDGE,"E10.sketch_text.stroke-126"),sQuery(id+"F4.wireOp",EDGE,"E10.sketch_text.stroke-127"),sQuery(id+"F4.wireOp",EDGE,"E10.sketch_text.stroke-128"),sQuery(id+"F4.wireOp",EDGE,"E10.sketch_text.stroke-129"),sQuery(id+"F4.wireOp",EDGE,"E10.sketch_text.stroke-130"),sQuery(id+"F4.wireOp",EDGE,"E10.sketch_text.stroke-131"),sQuery(id+"F4.wireOp",EDGE,"E10.sketch_text.stroke-132"),sQuery(id+"F4.wireOp",EDGE,"E10.sketch_text.stroke-133"),sQuery(id+"F4.wireOp",EDGE,"E10.sketch_text.stroke-134"),sQuery(id+"F4.wireOp",EDGE,"E10.sketch_text.stroke-135"),sQuery(id+"F4.wireOp",EDGE,"E10.sketch_text.stroke-136"),sQuery(id+"F4.wireOp",EDGE,"E10.sketch_text.stroke-137"),sQuery(id+"F4.wireOp",EDGE,"E10.sketch_text.stroke-138"),sQuery(id+"F4.wireOp",EDGE,"E10.sketch_text.stroke-139"),sQuery(id+"F4.wireOp",EDGE,"E10.sketch_text.stroke-140"),sQuery(id+"F4.wireOp",EDGE,"E10.sketch_text.stroke-141"),sQuery(id+"F4.wireOp",EDGE,"E10.sketch_text.stroke-142"),sQuery(id+"F4.wireOp",EDGE,"E10.sketch_text.stroke-143"),sQuery(id+"F4.wireOp",EDGE,"E10.sketch_text.stroke-144"),sQuery(id+"F4.wireOp",EDGE,"E10.sketch_text.stroke-145"),sQuery(id+"F4.wireOp",EDGE,"E10.sketch_text.stroke-146"),sQuery(id+"F4.wireOp",EDGE,"E10.sketch_text.stroke-147"),sQuery(id+"F4.wireOp",EDGE,"E10.sketch_text.stroke-148")])]});
            var Q9;
            Q9=makeQuery(id+"F5.opExtrude","SWEPT_BODY",BODY,{"disambiguationData":[OSD([sQuery(id+"F4.wireOp",EDGE,"E10.sketch_text.stroke-140"),sQuery(id+"F4.wireOp",EDGE,"E10.sketch_text.stroke-141"),sQuery(id+"F4.wireOp",EDGE,"E10.sketch_text.stroke-142"),sQuery(id+"F4.wireOp",EDGE,"E10.sketch_text.stroke-143"),sQuery(id+"F4.wireOp",EDGE,"E10.sketch_text.stroke-144"),sQuery(id+"F4.wireOp",EDGE,"E10.sketch_text.stroke-145"),sQuery(id+"F4.wireOp",EDGE,"E10.sketch_text.stroke-146"),sQuery(id+"F4.wireOp",EDGE,"E10.sketch_text.stroke-147"),sQuery(id+"F4.wireOp",EDGE,"E10.sketch_text.stroke-148"),sQuery(id+"F4.wireOp",EDGE,"E10.sketch_text.stroke-149"),sQuery(id+"F4.wireOp",EDGE,"E10.sketch_text.stroke-150"),sQuery(id+"F4.wireOp",EDGE,"E10.sketch_text.stroke-151"),sQuery(id+"F4.wireOp",EDGE,"E10.sketch_text.stroke-152"),sQuery(id+"F4.wireOp",EDGE,"E10.sketch_text.stroke-153"),sQuery(id+"F4.wireOp",EDGE,"E10.sketch_text.stroke-154"),sQuery(id+"F4.wireOp",EDGE,"E10.sketch_text.stroke-155"),sQuery(id+"F4.wireOp",EDGE,"E10.sketch_text.stroke-156"),sQuery(id+"F4.wireOp",EDGE,"E10.sketch_text.stroke-157"),sQuery(id+"F4.wireOp",EDGE,"E10.sketch_text.stroke-158"),sQuery(id+"F4.wireOp",EDGE,"E10.sketch_text.stroke-159"),sQuery(id+"F4.wireOp",EDGE,"E10.sketch_text.stroke-160"),sQuery(id+"F4.wireOp",EDGE,"E10.sketch_text.stroke-161"),sQuery(id+"F4.wireOp",EDGE,"E10.sketch_text.stroke-162"),sQuery(id+"F4.wireOp",EDGE,"E10.sketch_text.stroke-163"),sQuery(id+"F4.wireOp",EDGE,"E10.sketch_text.stroke-164"),sQuery(id+"F4.wireOp",EDGE,"E10.sketch_text.stroke-165"),sQuery(id+"F4.wireOp",EDGE,"E10.sketch_text.stroke-166"),sQuery(id+"F4.wireOp",EDGE,"E10.sketch_text.stroke-167")])]});
            var Q10;
            Q10=makeQuery(id+"F1.opExtrude","SWEPT_BODY",BODY,{"disambiguationData":[OSD([sQuery(id+"F0.wireOp",EDGE,"E2"),sQuery(id+"F0.wireOp",EDGE,"E3"),sQuery(id+"F0.wireOp",EDGE,"E4"),sQuery(id+"F0.wireOp",EDGE,"E5"),sQuery(id+"F0.wireOp",EDGE,"E6.MirrorCS"),sQuery(id+"F0.wireOp",EDGE,"E7.MirrorCS"),sQuery(id+"F0.wireOp",EDGE,"E8.MirrorCS")])]});
            booleanBodies(context, id + "F8", {"operationType" : BooleanOperationType.SUBTRACTION, "tools" : qUnion([Q0, Q1, Q2, Q3, Q4, Q5, Q6, Q7, Q8, Q9]), "targets" : qUnion([Q10])});
        }
    });
